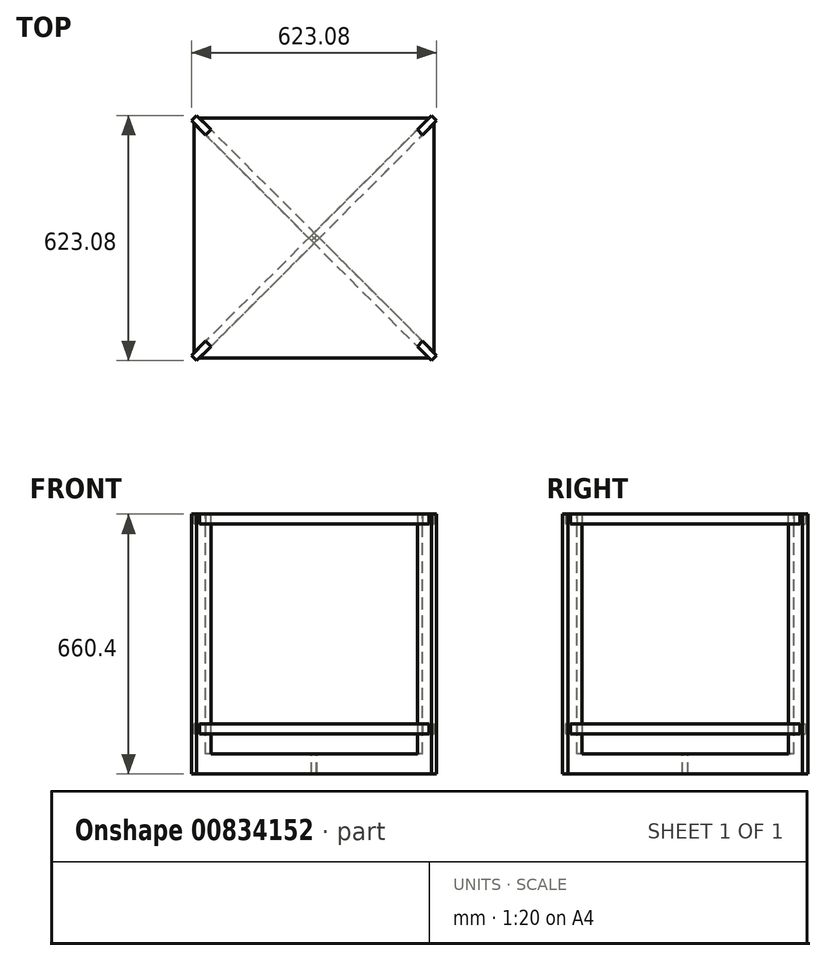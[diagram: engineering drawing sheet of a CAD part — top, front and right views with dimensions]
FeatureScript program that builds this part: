
annotation { "Feature Type Name" : "Feature", "Feature Type Description" : "" }
export const myFeature = defineFeature(function(context is Context, id is Id, definition is map)
    precondition{}
    {
        {
            var Q0;
            Q0=qCreatedBy(makeId("Top.planeOp"),FACE);
            var sketch = newSketch(context, id + "F0", { "sketchPlane" : qUnion([Q0])});
            skLineSegment(sketch, "E0.bottom", {"start": v(0, 0) * mm, "end": v(609.6, 0) * mm});
            skLineSegment(sketch, "E0.top", {"start": v(0, 609.6) * mm, "end": v(609.6, 609.6) * mm});
            skLineSegment(sketch, "E0.left", {"start": v(0, 0) * mm, "end": v(0, 609.6) * mm});
            skLineSegment(sketch, "E0.right", {"start": v(609.6, 0) * mm, "end": v(609.6, 609.6) * mm});
            skPoint(sketch, "E1", {"position": v(304.8, 304.8) * mm});
            skSolve(sketch);
        }
        {
            var Q0;
            Q0=qCreatedBy(makeId("Top.planeOp"),FACE);
            cPlane(context, id + "F1", {"entities" : qUnion([Q0]), "cplaneType" : CPlaneType.OFFSET, "offset" : 660.4 * mm, "width" : 152.4 * mm, "height" : 152.4 * mm});
        }
        {
            var Q0;
            Q0=qCreatedBy(id+"F1.planeOp",FACE);
            var sketch = newSketch(context, id + "F2", { "sketchPlane" : qUnion([Q0])});
            skLineSegment(sketch, "E2.bottom", {"start": v(0, 0) * mm, "end": v(609.6, 0) * mm});
            skLineSegment(sketch, "E2.top", {"start": v(0, 609.6) * mm, "end": v(609.6, 609.6) * mm});
            skLineSegment(sketch, "E2.left", {"start": v(0, 0) * mm, "end": v(0, 609.6) * mm});
            skLineSegment(sketch, "E2.right", {"start": v(609.6, 0) * mm, "end": v(609.6, 609.6) * mm});
            skLineSegment(sketch, "E3", {"start": v(-6.74, 602.86) * mm, "end": v(0, 609.6) * mm});
            skLineSegment(sketch, "E4", {"start": v(0, 609.6) * mm, "end": v(6.74, 616.34) * mm});
            skLineSegment(sketch, "E5", {"start": v(-6.74, 602.86) * mm, "end": v(29.19, 566.94) * mm});
            skLineSegment(sketch, "E6", {"start": v(29.19, 566.94) * mm, "end": v(42.66, 580.41) * mm});
            skLineSegment(sketch, "E7", {"start": v(42.66, 580.41) * mm, "end": v(6.74, 616.34) * mm});
            skPoint(sketch, "E8", {"position": v(304.8, 304.8) * mm});
            skSolve(sketch);
        }
        {
            var Q0;
            {var subQ6=sQuery(id+"F2.wireOp",EDGE,"E2.bottom");Q0=makeQuery(id+"F2.imprint","IMPRINT",FACE,{"disambiguationData":[TD([[makeQuery(id+"F2.imprint","IMPRINT",EDGE,{"derivedFrom":subQ6}),1.0]])]});}
            var sketch = newSketch(context, id + "F3", { "sketchPlane" : qUnion([Q0])});
            skPoint(sketch, "E9.0", {"position": v(3.37, 612.97) * mm});
            skLineSegment(sketch, "E10.0", {"start": v(0, 609.6) * mm, "end": v(6.74, 616.34) * mm});
            skLineSegment(sketch, "E11.0", {"start": v(-6.74, 602.86) * mm, "end": v(0, 609.6) * mm});
            skLineSegment(sketch, "E12.0", {"start": v(-6.74, 602.86) * mm, "end": v(29.19, 566.94) * mm});
            skLineSegment(sketch, "E13.0", {"start": v(29.19, 566.94) * mm, "end": v(42.66, 580.41) * mm});
            skLineSegment(sketch, "E14.0", {"start": v(42.66, 580.41) * mm, "end": v(6.74, 616.34) * mm});
            skSolve(sketch);
        }
        {
            var Q0;
            Q0=qSketchRegion(id+"F3",true);
            extrude(context, id + "F4", {"entities" : qUnion([Q0]), "oppositeDirection" : true, "depth" : 660.4 * mm});
        }
        {
            var Q0;
            Q0=makeQuery(id+"F4.opExtrude","SWEPT_FACE",FACE,{"disambiguationData":[OSD([sQuery(id+"F3.wireOp",EDGE,"E13.0")])]});
            var sketch = newSketch(context, id + "F5", { "sketchPlane" : qUnion([Q0])});
            skLineSegment(sketch, "E15.bottom", {"start": v(440.58, 0) * mm, "end": v(421.53, 0) * mm});
            skLineSegment(sketch, "E15.top", {"start": v(440.58, 50.8) * mm, "end": v(421.53, 50.8) * mm});
            skLineSegment(sketch, "E15.left", {"start": v(440.58, 0) * mm, "end": v(440.58, 50.8) * mm});
            skLineSegment(sketch, "E15.right", {"start": v(421.53, 0) * mm, "end": v(421.53, 50.8) * mm});
            skSolve(sketch);
        }
        {
            var Q0;
            Q0=makeQuery(id+"F5.imprint","IMPRINT",FACE,{"disambiguationData":[TD([[makeQuery(id+"F5.imprint","IMPRINT",EDGE,{"derivedFrom":sQuery(id+"F5.wireOp",EDGE,"E15.bottom")}),1.0]])]});
            extrude(context, id + "F6", {"entities" : qUnion([Q0]), "operationType" : NewBodyOperationType.ADD, "depth" : 380.24 * mm});
        }
        {
            var Q0;
            Q0=qCreatedBy(makeId("Right.planeOp"),FACE);
            cPlane(context, id + "F7", {"entities" : qUnion([Q0]), "cplaneType" : CPlaneType.OFFSET, "offset" : 304.8 * mm, "width" : 152.4 * mm, "height" : 152.4 * mm});
        }
        {
            var Q0;
            Q0=qCreatedBy(id+"F7.planeOp",FACE);
            var sketch = newSketch(context, id + "F8", { "sketchPlane" : qUnion([Q0])});
            skLineSegment(sketch, "E16", {"start": v(304.8, 1072.96) * mm, "end": v(304.8, -266.55) * mm});
            skSolve(sketch);
        }
        {
            var Q0;
            Q0=makeQuery(id+"F4.opExtrude","SWEPT_BODY",BODY,{"disambiguationData":[OSD([sQuery(id+"F3.wireOp",EDGE,"E10.0"),sQuery(id+"F3.wireOp",EDGE,"E11.0"),sQuery(id+"F3.wireOp",EDGE,"E12.0"),sQuery(id+"F3.wireOp",EDGE,"E13.0"),sQuery(id+"F3.wireOp",EDGE,"E14.0")])]});
            var Q1;
            Q1=sQuery(id+"F8.wireOp",EDGE,"E16");
            circularPattern(context, id + "F9", {"entities" : qUnion([Q0]), "axis" : qUnion([Q1]), "angle" : 90 * degree, "instanceCount" : 4});
        }
        {
            var Q0;
            Q0=qCreatedBy(makeId("Top.planeOp"),FACE);
            cPlane(context, id + "F10", {"entities" : qUnion([Q0]), "cplaneType" : CPlaneType.OFFSET, "offset" : 101.6 * mm, "width" : 152.4 * mm, "height" : 152.4 * mm});
        }
        {
            var Q0;
            Q0=qCreatedBy(id+"F10.planeOp",FACE);
            var sketch = newSketch(context, id + "F11", { "sketchPlane" : qUnion([Q0])});
            skLineSegment(sketch, "E17.bottom", {"start": v(13.47, 0) * mm, "end": v(596.13, 0) * mm});
            skLineSegment(sketch, "E17.top", {"start": v(13.47, 609.6) * mm, "end": v(596.13, 609.6) * mm});
            skLineSegment(sketch, "E17.left", {"start": v(0, 13.47) * mm, "end": v(0, 596.13) * mm});
            skLineSegment(sketch, "E17.right", {"start": v(609.6, 13.47) * mm, "end": v(609.6, 596.13) * mm});
            skLineSegment(sketch, "E18", {"start": v(42.66, 580.41) * mm, "end": v(29.19, 566.94) * mm});
            skLineSegment(sketch, "E19", {"start": v(42.66, 580.41) * mm, "end": v(13.47, 609.6) * mm});
            skLineSegment(sketch, "E20", {"start": v(29.19, 566.94) * mm, "end": v(0, 596.13) * mm});
            skLineSegment(sketch, "E21", {"start": v(566.94, 580.41) * mm, "end": v(580.41, 566.94) * mm});
            skLineSegment(sketch, "E22", {"start": v(566.94, 580.41) * mm, "end": v(596.13, 609.6) * mm});
            skLineSegment(sketch, "E23", {"start": v(580.41, 566.94) * mm, "end": v(609.6, 596.13) * mm});
            skLineSegment(sketch, "E24", {"start": v(566.94, 29.19) * mm, "end": v(580.41, 42.66) * mm});
            skLineSegment(sketch, "E25", {"start": v(580.41, 42.66) * mm, "end": v(609.6, 13.47) * mm});
            skLineSegment(sketch, "E26", {"start": v(566.94, 29.19) * mm, "end": v(596.13, 0) * mm});
            skLineSegment(sketch, "E27", {"start": v(29.19, 42.66) * mm, "end": v(42.66, 29.19) * mm});
            skLineSegment(sketch, "E28", {"start": v(29.19, 42.66) * mm, "end": v(0, 13.47) * mm});
            skLineSegment(sketch, "E29", {"start": v(42.66, 29.19) * mm, "end": v(13.47, 0) * mm});
            skPoint(sketch, "E30.orphan", {"position": v(0, 0) * mm});
            skSolve(sketch);
        }
        {
            var Q0;
            Q0=makeQuery(id+"F11.imprint","IMPRINT",FACE,{"disambiguationData":[TD([[makeQuery(id+"F11.imprint","IMPRINT",EDGE,{"derivedFrom":sQuery(id+"F11.wireOp",EDGE,"E17.bottom")}),1.0]])]});
            extrude(context, id + "F12", {"entities" : qUnion([Q0]), "depth" : 25.4 * mm});
        }
        {
            var Q0;
            Q0=makeQuery(id+"F12.opExtrude","SWEPT_BODY",BODY,{"disambiguationData":[OSD([sQuery(id+"F11.wireOp",EDGE,"E17.bottom"),sQuery(id+"F11.wireOp",EDGE,"E17.top"),sQuery(id+"F11.wireOp",EDGE,"E17.left"),sQuery(id+"F11.wireOp",EDGE,"E17.right"),sQuery(id+"F11.wireOp",EDGE,"E18"),sQuery(id+"F11.wireOp",EDGE,"E19"),sQuery(id+"F11.wireOp",EDGE,"E20"),sQuery(id+"F11.wireOp",EDGE,"E21"),sQuery(id+"F11.wireOp",EDGE,"E22"),sQuery(id+"F11.wireOp",EDGE,"E23"),sQuery(id+"F11.wireOp",EDGE,"E24"),sQuery(id+"F11.wireOp",EDGE,"E25"),sQuery(id+"F11.wireOp",EDGE,"E26"),sQuery(id+"F11.wireOp",EDGE,"E27"),sQuery(id+"F11.wireOp",EDGE,"E28"),sQuery(id+"F11.wireOp",EDGE,"E29")])]});
            transform(context, id + "F13", {"entities" : qUnion([Q0]), "transformType" : TransformType.TRANSLATION_3D, "dx" : 0 * mm, "dy" : 0 * mm, "dz" : 533.4 * mm, "makeCopy" : true});
        }
    });
